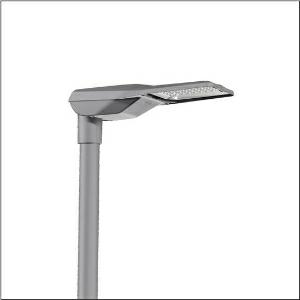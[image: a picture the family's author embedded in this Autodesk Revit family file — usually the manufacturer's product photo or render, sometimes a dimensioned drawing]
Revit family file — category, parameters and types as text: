
# Revit family: streetlight_sl_21_iq_mini___st1_5a_5xe2p31g08hb_126e
name_source: partatom
category: Lighting Fixtures
units: mm (PartAtom-declared; Revit-internal decimal feet)

## family parameters
Cut with Voids When Loaded = No
Host = Face
Light Source = No
Part Type = Normal
Room Calculation Point = No
Round Connector Dimension = Use Diameter
Shared = No

## types (1)
- --- (1 x LED, 9290 lm, 70.9 W, 3000K)
    Apparent Load = 71 VA
    CIE Flux Codes = 22 53 95 100 100
    Color Rendering = 70
    Color Temperature = 3000K
    Default Elevation = 1800 mm
    Description = Streetlight SL 21 iQ mini, mast luminaire, primary light control with lens, of PMMA, primary optical cover: cover, of toughened safety glass, transparent, light distribution: ST1.5a, light emission: direct distribution, primary light characteristic: asymmetric, installation type: post-top, side-entry, LED, High Power LED, rated luminous flux: 9.290lm, luminous efficacy: 131lm/W, light colour: 730, colour temperature: 3000K, control gear: iQ Street-Remote, control: Street-Remote, Auto-Match, Temp-Guard, Lumen-Switch, Night-Set, Smart-Wire, Light-Fading, Desk-Remote (wireless, voltage-free reading and setting of iQ features in the workshop via application-optimized NFC function/RFID function), optimised constant luminous flux control (CLO 2.0), pre-setting: linear dimming characteristic, mains connection: 220..240V, AC, 50/60Hz, start of lifetime: 71W, end of service life: 75W, reduction: 31W, luminaire housing, of diecast aluminium, powder-coated, SITECO metallic grey (DB 702S), corrosivity category C5 high according to DIN EN ISO 12944, please order mast flange separately, inclination adjustable: 0°, 5°, 10°, 15°, sealing non-destructively replaceable, multi-level sealing system, length: 628mm, width: 235mm, height: 110mm, mast flange for spigot size: 42mm (side-entry): 5XC10008XM4, 60/48mm (side-entry/post-top): 5XC10108XM2, 76/60mm (side-entry/post-top): 5XC10108XM1, mounting height: 4..8m, protection rating (complete): IP66, insulation class (complete): insulation class II (safety insulation), certification: CE, ENEC, ENEC+, VDE, impact resistance: IK10, permissible operating ambient temperature for outdoor applications: -40..+50°C, standard-compliant lighting for roads and squares, packaging unit: 1 piece

Light Distribution: ST1.5a
    Height = 110 mm
    Lamp = 1 x LED
    Lamp Light Flux = 9290 lm
    Lamp Power = 70.9 W
    Lamp count = 1
    Length = 625 mm
    Luminous efficacy = 131 lm/W
    Manufacturer = Siteco
    ModVariant = No
    Model = 5XE2P31G08HB
    Number of Poles = 1
    OnlyDefault = Yes
    Power Factor = 1
    Product Name = Streetlight SL 21 iQ mini | ST1.5a
    Product group = mast luminaire | pylon top
    ProductGroupID = 6100
    Protection Class = Protection class II
    Protection Degree = IP 66
    RLX_Detail_Level = 1
    RLX_Emergency_Light_Flux = 0 lm
    RLX_Emergency_Type = 0
    RLX_Emergency_Type_DB = No
    RlxData = <blob elided: 29861 chars, md5=2fbe6ee6>
    Socket = socket
    Standby Power = 0 W
    System Light Flux = 9290 lm
    System Power = 71 W
    Type Comments = factory setting: luminous flux: 100 % | dim-lin: 254 | 711 mA
    Type Image = l_1003519.jpg
    URL = http://relux.com
    VarID = @adj_156539
    Voltage = 0 V
    Weight = 0.00 kg
    Width = 234 mm

## geometry (parser evidence)
native form markers: Blend x4, Sweep x8
no freeform markers — native parametric forms only
